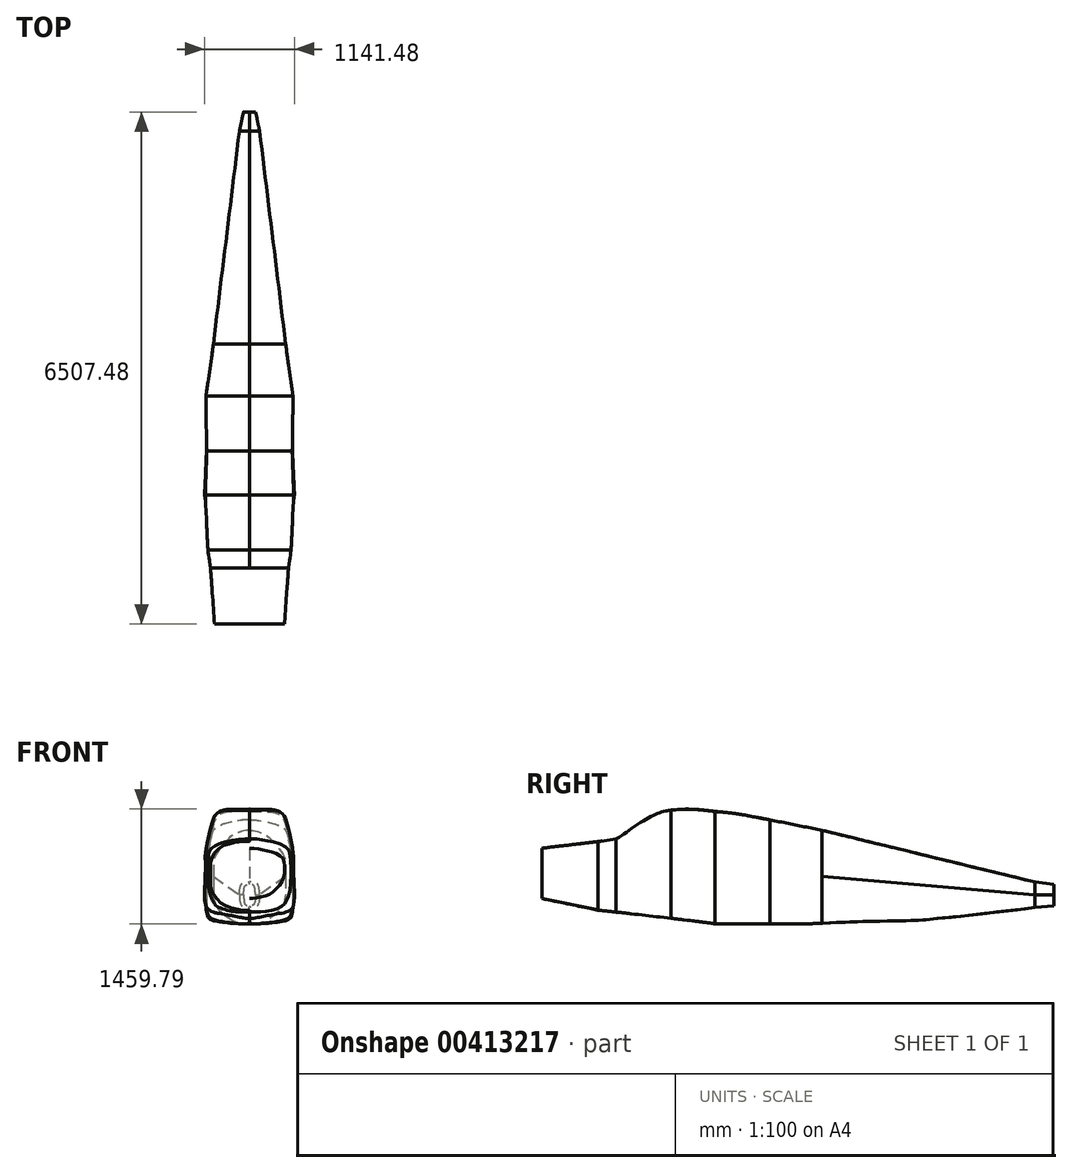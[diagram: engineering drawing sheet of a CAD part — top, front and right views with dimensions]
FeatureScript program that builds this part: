
annotation { "Feature Type Name" : "Feature", "Feature Type Description" : "" }
export const myFeature = defineFeature(function(context is Context, id is Id, definition is map)
    precondition{}
    {
        {
            var Q0;
            Q0=qCreatedBy(makeId("Right.planeOp"),FACE);
            var sketch = newSketch(context, id + "F0", { "sketchPlane" : qUnion([Q0])});
            skLineSegment(sketch, "E0.bottom", {"start": v(0, 664.6) * mm, "end": v(7102.65, 664.6) * mm});
            skLineSegment(sketch, "E0.top", {"start": v(0, -785.51) * mm, "end": v(7102.65, -785.51) * mm});
            skLineSegment(sketch, "E0.left", {"start": v(0, 664.6) * mm, "end": v(0, -785.51) * mm});
            skLineSegment(sketch, "E0.right", {"start": v(7102.65, 664.6) * mm, "end": v(7102.65, -785.51) * mm});
            skLineSegment(sketch, "E1", {"start": v(443.28, 664.6) * mm, "end": v(443.28, -785.51) * mm});
            skLineSegment(sketch, "E2", {"start": v(1215.1, 664.6) * mm, "end": v(1215.1, -785.51) * mm});
            skLineSegment(sketch, "E3", {"start": v(1422.4, 664.6) * mm, "end": v(1422.4, -785.51) * mm});
            skLineSegment(sketch, "E4", {"start": v(2120.9, 664.6) * mm, "end": v(2120.9, -785.51) * mm});
            skLineSegment(sketch, "E5", {"start": v(2679.7, -785.51) * mm, "end": v(2679.7, 664.6) * mm});
            skLineSegment(sketch, "E6", {"start": v(4038.6, -785.51) * mm, "end": v(4038.6, 664.6) * mm});
            skLineSegment(sketch, "E7", {"start": v(6743.7, -785.51) * mm, "end": v(6743.7, 664.6) * mm});
            skSolve(sketch);
        }
        {
            var Q0;
            Q0=qCreatedBy(makeId("Right.planeOp"),FACE);
            var sketch = newSketch(context, id + "F1", { "sketchPlane" : qUnion([Q0])});
            skLineSegment(sketch, "E8", {"start": v(1193.8, 265.93) * mm, "end": v(1193.8, -604.42) * mm, "construction": true});
            skPoint(sketch, "E9.0", {"position": v(2120.9, 664.6) * mm});
            skLineSegment(sketch, "E10", {"start": v(2120.9, 664.6) * mm, "end": v(2120.9, -709.04) * mm, "construction": true});
            skLineSegment(sketch, "E11", {"start": v(2681.49, 648.53) * mm, "end": v(2681.49, -773.88) * mm, "construction": true});
            skLineSegment(sketch, "E12", {"start": v(3378.2, 541.47) * mm, "end": v(3378.2, -781.53) * mm, "construction": true});
            skLineSegment(sketch, "E13", {"start": v(4038.6, 407.3) * mm, "end": v(4038.6, -774.77) * mm, "construction": true});
            skLineSegment(sketch, "E14", {"start": v(6743.7, -248.1) * mm, "end": v(6743.7, -572.47) * mm, "construction": true});
            skLineSegment(sketch, "E15", {"start": v(6985, -277.2) * mm, "end": v(6985, -542.5) * mm, "construction": true});
            skLineSegment(sketch, "E16", {"start": v(1422.4, 302.03) * mm, "end": v(1422.4, -628.4) * mm, "construction": true});
            skSolve(sketch);
        }
        {
            var Q0;
            Q0=qCreatedBy(makeId("Front.planeOp"),FACE);
            cPlane(context, id + "F2", {"entities" : qUnion([Q0]), "cplaneType" : CPlaneType.OFFSET, "offset" : 477.52 * mm, "oppositeDirection" : true, "width" : 152.4 * mm, "height" : 152.4 * mm});
        }
        {
            var Q0;
            Q0=qCreatedBy(id+"F2.planeOp",FACE);
            var sketch = newSketch(context, id + "F3", { "sketchPlane" : qUnion([Q0])});
            skLineSegment(sketch, "E17", {"start": v(0, 424.34) * mm, "end": v(0, -539.78) * mm, "construction": true});
            skFitSpline(sketch, "E18", {"points": [v(0, 182.3) * mm, v(-107.19, 174.3) * mm, v(-211.2, 152.3) * mm, v(-325.22, 122.3) * mm, v(-413.23, 66.3) * mm, v(-443.23, 0) * mm, v(-443.23, -75.73) * mm, v(-441.23, -153.74) * mm, v(-407.23, -249.75) * mm, v(-343.22, -329.76) * mm, v(-259.2, -399.77) * mm, v(-165.2, -431.77) * mm, v(-58.44, -456.1) * mm, v(0, -457.77) * mm], "startDerivative": vector(-1334.66, 9.94) * mm, "endDerivative": vector(885.54, -12.67) * mm});
            skFitSpline(sketch, "E19.MirrorCS", {"points": [v(0, 182.3) * mm, v(107.19, 174.3) * mm, v(211.2, 152.3) * mm, v(325.22, 122.3) * mm, v(413.23, 66.3) * mm, v(443.23, 0) * mm, v(443.23, -75.73) * mm, v(441.23, -153.74) * mm, v(407.23, -249.75) * mm, v(343.22, -329.76) * mm, v(259.2, -399.77) * mm, v(165.2, -431.77) * mm, v(58.44, -456.1) * mm, v(0, -457.77) * mm], "startDerivative": vector(1334.66, 9.94) * mm, "endDerivative": vector(-885.54, -12.67) * mm});
            skSolve(sketch);
        }
        {
            var Q0;
            Q0=qCreatedBy(makeId("Front.planeOp"),FACE);
            cPlane(context, id + "F4", {"entities" : qUnion([Q0]), "cplaneType" : CPlaneType.OFFSET, "offset" : 1193.8 * mm, "oppositeDirection" : true, "width" : 152.4 * mm, "height" : 152.4 * mm});
        }
        {
            var Q0;
            Q0=qCreatedBy(id+"F4.planeOp",FACE);
            var sketch = newSketch(context, id + "F5", { "sketchPlane" : qUnion([Q0])});
            skPoint(sketch, "E20.0", {"position": v(0, 265.93) * mm});
            skPoint(sketch, "E21.0", {"position": v(0, -604.42) * mm});
            skLineSegment(sketch, "E22", {"start": v(0, 497.9) * mm, "end": v(0, -830.14) * mm, "construction": true});
            skFitSpline(sketch, "E23", {"points": [v(0, 265.93) * mm, v(-117.24, 265.93) * mm, v(-218.7, 247.73) * mm, v(-365.7, 195.3) * mm, v(-467.13, 84.77) * mm, v(-493.34, -18.93) * mm, v(-494.48, -237.72) * mm, v(-492.2, -322.05) * mm, v(-473.96, -381.3) * mm, v(-394.2, -483.86) * mm, v(-291.8, -554.77) * mm, v(-118.4, -602.02) * mm, v(-65.62, -605.24) * mm, v(0, -604.42) * mm], "startDerivative": vector(-1503.76, -16.45) * mm, "endDerivative": vector(927.22, -11.34) * mm});
            skFitSpline(sketch, "E24.MirrorCS", {"points": [v(0, 265.93) * mm, v(117.24, 265.93) * mm, v(218.7, 247.73) * mm, v(365.7, 195.3) * mm, v(467.13, 84.77) * mm, v(493.34, -18.93) * mm, v(494.48, -237.72) * mm, v(492.2, -322.05) * mm, v(473.96, -381.3) * mm, v(394.2, -483.86) * mm, v(291.8, -554.77) * mm, v(118.4, -602.02) * mm, v(65.62, -605.24) * mm, v(0, -604.42) * mm], "startDerivative": vector(1503.76, -16.45) * mm, "endDerivative": vector(-927.22, -11.34) * mm});
            skSolve(sketch);
        }
        {
            var Q0;
            Q0=qCreatedBy(makeId("Right.planeOp"),FACE);
            var sketch = newSketch(context, id + "F6", { "sketchPlane" : qUnion([Q0])});
            skPoint(sketch, "E25.0", {"position": v(477.52, -457.77) * mm});
            skPoint(sketch, "E26.0", {"position": v(1193.8, -604.42) * mm});
            skLineSegment(sketch, "E27", {"start": v(477.52, -457.77) * mm, "end": v(578.9, -487.9) * mm});
            skLineSegment(sketch, "E28", {"start": v(578.9, -487.9) * mm, "end": v(709.03, -514.45) * mm});
            skLineSegment(sketch, "E29", {"start": v(709.03, -514.45) * mm, "end": v(886.96, -554.29) * mm});
            skLineSegment(sketch, "E30", {"start": v(886.96, -554.29) * mm, "end": v(1006.47, -583.5) * mm});
            skLineSegment(sketch, "E31", {"start": v(1006.47, -583.5) * mm, "end": v(1091.45, -607.4) * mm});
            skLineSegment(sketch, "E32", {"start": v(1091.45, -607.4) * mm, "end": v(1193.8, -604.42) * mm});
            skSolve(sketch);
        }
        {
            var Q0;
            Q0 = qSketchRegion(id + "F3", true);
            var Q1;
            Q1 = qSketchRegion(id + "F5", true);
            var Q2;
            Q2 = qConstructionFilter(qBodyType(qCreatedBy(id + "F6" ,EDGE), BodyType.WIRE), ConstructionObject.NO);
            loft(context, id + "F7", {"sheetProfilesArray" : [{ "sheetProfileEntities" : qUnion([Q0]) }, { "sheetProfileEntities" : qUnion([Q1]) }], "guidesArray" : [{ "guideEntities" : qUnion([Q2]), "guideDerivativeType" : LoftGuideDerivativeType.DEFAULT, "guideDerivativeMagnitude" : 1 }]});
        }
        {
            var Q0;
            Q0=qCreatedBy(makeId("Front.planeOp"),FACE);
            cPlane(context, id + "F8", {"entities" : qUnion([Q0]), "cplaneType" : CPlaneType.OFFSET, "offset" : 2120.9 * mm, "oppositeDirection" : true, "width" : 152.4 * mm, "height" : 152.4 * mm});
        }
        {
            var Q0;
            Q0=qCreatedBy(id+"F8.planeOp",FACE);
            var sketch = newSketch(context, id + "F9", { "sketchPlane" : qUnion([Q0])});
            skPoint(sketch, "E33.0", {"position": v(0, 664.6) * mm});
            skPoint(sketch, "E34.0", {"position": v(0, -709.04) * mm});
            skLineSegment(sketch, "E35", {"start": v(0, 971.77) * mm, "end": v(0, -1592.86) * mm, "construction": true});
            skFitSpline(sketch, "E36", {"points": [v(0, 664.6) * mm, v(-101.29, 664.6) * mm, v(-256.4, 664.6) * mm, v(-374.13, 647.55) * mm, v(-435.8, 602.7) * mm, v(-473.18, 499.92) * mm, v(-521.77, 320.52) * mm, v(-561.01, 81.31) * mm, v(-561.01, 21.5) * mm, v(-564.75, -225.17) * mm, v(-564.75, -511.18) * mm, v(-511.32, -608.6) * mm, v(-329.03, -655.75) * mm, v(-149.88, -690.32) * mm, v(0, -709.04) * mm], "startDerivative": vector(-1623.74, -9.76) * mm, "endDerivative": vector(2155.82, 3.58) * mm});
            skFitSpline(sketch, "E37.MirrorCS", {"points": [v(0, 664.6) * mm, v(101.29, 664.6) * mm, v(256.4, 664.6) * mm, v(374.13, 647.55) * mm, v(435.8, 602.7) * mm, v(473.18, 499.92) * mm, v(521.77, 320.52) * mm, v(561.01, 81.31) * mm, v(561.01, 21.5) * mm, v(564.75, -225.17) * mm, v(564.75, -511.18) * mm, v(511.32, -608.6) * mm, v(329.03, -655.75) * mm, v(149.88, -690.32) * mm, v(0, -709.04) * mm], "startDerivative": vector(1623.74, -9.76) * mm, "endDerivative": vector(-2155.82, 3.58) * mm});
            skSolve(sketch);
        }
        {
            var Q0;
            Q0=qCreatedBy(makeId("Front.planeOp"),FACE);
            cPlane(context, id + "F10", {"entities" : qUnion([Q0]), "cplaneType" : CPlaneType.OFFSET, "offset" : 2679.7 * mm, "oppositeDirection" : true, "width" : 152.4 * mm, "height" : 152.4 * mm});
        }
        {
            var Q0;
            Q0=qCreatedBy(id+"F10.planeOp",FACE);
            var sketch = newSketch(context, id + "F11", { "sketchPlane" : qUnion([Q0])});
            skPoint(sketch, "E38.0", {"position": v(0, 648.53) * mm});
            skPoint(sketch, "E39.0", {"position": v(0, -773.88) * mm});
            skFitSpline(sketch, "E40", {"points": [v(0, 648.53) * mm, v(-140.26, 646.75) * mm, v(-333.17, 631.31) * mm, v(-426.03, 561.67) * mm, v(-474.4, 414.64) * mm, v(-534.2, 101.76) * mm, v(-540.4, 33.51) * mm, v(-542.02, -96.63) * mm, v(-542.7, -300.13) * mm, v(-545, -544) * mm, v(-518.89, -679.55) * mm, v(-441.96, -729.72) * mm, v(-281.91, -759.82) * mm, v(-86.3, -778.97) * mm, v(0, -773.88) * mm], "startDerivative": vector(-2067.33, -24.6) * mm, "endDerivative": vector(1428.64, 166.52) * mm});
            skFitSpline(sketch, "E41.MirrorCS", {"points": [v(0, 648.53) * mm, v(140.26, 646.75) * mm, v(333.17, 631.31) * mm, v(426.03, 561.67) * mm, v(474.4, 414.64) * mm, v(534.2, 101.76) * mm, v(540.4, 33.51) * mm, v(542.02, -96.63) * mm, v(542.7, -300.13) * mm, v(545, -544) * mm, v(518.89, -679.55) * mm, v(441.96, -729.72) * mm, v(281.91, -759.82) * mm, v(86.3, -778.97) * mm, v(0, -773.88) * mm], "startDerivative": vector(2067.33, -24.6) * mm, "endDerivative": vector(-1428.64, 166.52) * mm});
            skSolve(sketch);
        }
        {
            var Q0;
            Q0=qCreatedBy(makeId("Right.planeOp"),FACE);
            var sketch = newSketch(context, id + "F12", { "sketchPlane" : qUnion([Q0])});
            skPoint(sketch, "E42.0", {"position": v(2120.9, 664.6) * mm});
            skPoint(sketch, "E43.0", {"position": v(2679.7, 648.53) * mm});
            skFitSpline(sketch, "E44", {"points": [v(2679.7, 648.53) * mm, v(2506.44, 669.53) * mm, v(2270.09, 677.5) * mm, v(2120.9, 664.6) * mm], "startDerivative": vector(-512.84, 70.22) * mm, "endDerivative": vector(-464.5, -49.21) * mm});
            skSolve(sketch);
        }
        {
            var Q0;
            Q0 = qSketchRegion(id + "F9", true);
            var Q1;
            Q1 = qSketchRegion(id + "F11", true);
            var Q2;
            Q2 = qConstructionFilter(qBodyType(qCreatedBy(id + "F12" ,EDGE), BodyType.WIRE), ConstructionObject.NO);
            loft(context, id + "F13", {"addGuides" : true, "sheetProfilesArray" : [{ "sheetProfileEntities" : qUnion([Q0]) }, { "sheetProfileEntities" : qUnion([Q1]) }], "guidesArray" : [{ "guideEntities" : qUnion([Q2]), "guideDerivativeType" : LoftGuideDerivativeType.DEFAULT, "guideDerivativeMagnitude" : 1 }]});
        }
        {
            var Q0;
            Q0=qCreatedBy(makeId("Front.planeOp"),FACE);
            cPlane(context, id + "F14", {"entities" : qUnion([Q0]), "cplaneType" : CPlaneType.OFFSET, "offset" : 3378.2 * mm, "oppositeDirection" : true, "width" : 152.4 * mm, "height" : 152.4 * mm});
        }
        {
            var Q0;
            Q0=qCreatedBy(id+"F14.planeOp",FACE);
            var sketch = newSketch(context, id + "F15", { "sketchPlane" : qUnion([Q0])});
            skPoint(sketch, "E45.0", {"position": v(0, 541.47) * mm});
            skPoint(sketch, "E46.0", {"position": v(0, -781.53) * mm});
            skFitSpline(sketch, "E47", {"points": [v(0, 541.47) * mm, v(-60.52, 541.47) * mm, v(-174.88, 526.9) * mm, v(-293.18, 499.3) * mm, v(-386.5, 462.5) * mm, v(-445.65, 427) * mm, v(-475.89, 378.37) * mm, v(-511.38, 212.75) * mm, v(-541.6, 16.9) * mm, v(-549.5, -105.34) * mm, v(-552.62, -339.82) * mm, v(-551.68, -522.73) * mm, v(-538.67, -662.15) * mm, v(-499.63, -719.78) * mm, v(-408.54, -749.52) * mm, v(-198.49, -773.69) * mm, v(0, -781.53) * mm], "startDerivative": vector(-1297.49, 46.78) * mm, "endDerivative": vector(2468.79, -52.6) * mm});
            skFitSpline(sketch, "E48.MirrorCS", {"points": [v(0, 541.47) * mm, v(60.52, 541.47) * mm, v(174.88, 526.9) * mm, v(293.18, 499.3) * mm, v(386.5, 462.5) * mm, v(445.65, 427) * mm, v(475.89, 378.37) * mm, v(511.38, 212.75) * mm, v(541.6, 16.9) * mm, v(549.5, -105.34) * mm, v(552.62, -339.82) * mm, v(551.68, -522.73) * mm, v(538.67, -662.15) * mm, v(499.63, -719.78) * mm, v(408.54, -749.52) * mm, v(198.49, -773.69) * mm, v(0, -781.53) * mm], "startDerivative": vector(1297.49, 46.78) * mm, "endDerivative": vector(-2468.79, -52.6) * mm});
            skSolve(sketch);
        }
        {
            var Q0;
            Q0=qCreatedBy(makeId("Right.planeOp"),FACE);
            var sketch = newSketch(context, id + "F16", { "sketchPlane" : qUnion([Q0])});
            skPoint(sketch, "E49.0", {"position": v(2679.7, 648.53) * mm});
            skPoint(sketch, "E50.0", {"position": v(3378.2, 541.47) * mm});
            skFitSpline(sketch, "E51", {"points": [v(2679.7, 648.53) * mm, v(2902.66, 626.6) * mm, v(3105.88, 593.1) * mm, v(3285.74, 558.17) * mm, v(3378.2, 541.47) * mm], "startDerivative": vector(795.05, -63.4) * mm, "endDerivative": vector(532.18, -90) * mm});
            skSolve(sketch);
        }
        {
            var Q0;
            Q0 = qSketchRegion(id + "F11", true);
            var Q1;
            Q1 = qSketchRegion(id + "F15", true);
            var Q2;
            Q2 = qConstructionFilter(qBodyType(qCreatedBy(id + "F16" ,EDGE), BodyType.WIRE), ConstructionObject.NO);
            loft(context, id + "F17", {"addGuides" : true, "sheetProfilesArray" : [{ "sheetProfileEntities" : qUnion([Q0]) }, { "sheetProfileEntities" : qUnion([Q1]) }], "guidesArray" : [{ "guideEntities" : qUnion([Q2]), "guideDerivativeType" : LoftGuideDerivativeType.DEFAULT, "guideDerivativeMagnitude" : 1 }]});
        }
        {
            var Q0;
            Q0=qCreatedBy(makeId("Front.planeOp"),FACE);
            cPlane(context, id + "F18", {"entities" : qUnion([Q0]), "cplaneType" : CPlaneType.OFFSET, "offset" : 4038.6 * mm, "oppositeDirection" : true, "width" : 152.4 * mm, "height" : 152.4 * mm});
        }
        {
            var Q0;
            Q0=qCreatedBy(makeId("Top.planeOp"),FACE);
            var sketch = newSketch(context, id + "F19", { "sketchPlane" : qUnion([Q0])});
            skLineSegment(sketch, "E52", {"start": v(0, 4038.6) * mm, "end": v(495.66, 4038.6) * mm, "construction": true});
            skLineSegment(sketch, "E53", {"start": v(495.66, 4038.6) * mm, "end": v(-456.85, 4038.6) * mm, "construction": true});
            skLineSegment(sketch, "E54", {"start": v(0, 6743.7) * mm, "end": v(-127, 6743.7) * mm, "construction": true});
            skLineSegment(sketch, "E55", {"start": v(0, 6743.7) * mm, "end": v(127, 6743.7) * mm, "construction": true});
            skLineSegment(sketch, "E56", {"start": v(0, 6743.7) * mm, "end": v(0, 7109.15) * mm, "construction": true});
            skLineSegment(sketch, "E57", {"start": v(0, 7001.4) * mm, "end": v(-76.2, 7001.4) * mm, "construction": true});
            skLineSegment(sketch, "E58", {"start": v(0, 7001.4) * mm, "end": v(76.2, 7001.4) * mm, "construction": true});
            skSolve(sketch);
        }
        {
            var Q0;
            Q0=qCreatedBy(id+"F18.planeOp",FACE);
            var sketch = newSketch(context, id + "F20", { "sketchPlane" : qUnion([Q0])});
            skPoint(sketch, "E59.0", {"position": v(-456.85, 0) * mm});
            skPoint(sketch, "E60.0", {"position": v(495.66, 0) * mm});
            skPoint(sketch, "E61.0", {"position": v(0, 407.3) * mm});
            skPoint(sketch, "E62.0", {"position": v(0, -774.77) * mm});
            skFitSpline(sketch, "E63", {"points": [v(0, 407.3) * mm, v(-51.47, 407.3) * mm, v(-149.27, 376.32) * mm, v(-240.24, 326.29) * mm, v(-324.39, 239.86) * mm, v(-424.46, 103.4) * mm, v(-456.85, 0) * mm, v(-456.85, -224.1) * mm, v(-456.85, -387.85) * mm, v(-424.46, -551.6) * mm, v(-347.13, -642.57) * mm, v(-247.06, -715.35) * mm, v(-142.44, -765.38) * mm, v(0, -774.77) * mm], "startDerivative": vector(-972.04, 89.96) * mm, "endDerivative": vector(1842.9, 24.98) * mm});
            skLineSegment(sketch, "E64", {"start": v(0, 407.3) * mm, "end": v(0, -774.77) * mm, "construction": true});
            skFitSpline(sketch, "E65.MirrorCS", {"points": [v(0, 407.3) * mm, v(51.47, 407.3) * mm, v(149.27, 376.32) * mm, v(240.24, 326.29) * mm, v(324.39, 239.86) * mm, v(424.46, 103.4) * mm, v(456.85, 0) * mm, v(456.85, -224.1) * mm, v(456.85, -387.85) * mm, v(424.46, -551.6) * mm, v(347.13, -642.57) * mm, v(247.06, -715.35) * mm, v(142.44, -765.38) * mm, v(0, -774.77) * mm], "startDerivative": vector(972.04, 89.96) * mm, "endDerivative": vector(-1842.9, 24.98) * mm});
            skSolve(sketch);
        }
        {
            var Q0;
            Q0 = qSketchRegion(id + "F15", true);
            var Q1;
            Q1 = qSketchRegion(id + "F20", true);
            loft(context, id + "F21", {"sheetProfilesArray" : [{ "sheetProfileEntities" : qUnion([Q0]) }, { "sheetProfileEntities" : qUnion([Q1]) }]});
        }
        {
            var Q0;
            Q0=qCreatedBy(makeId("Front.planeOp"),FACE);
            cPlane(context, id + "F22", {"entities" : qUnion([Q0]), "cplaneType" : CPlaneType.OFFSET, "offset" : 6743.7 * mm, "oppositeDirection" : true, "width" : 152.4 * mm, "height" : 152.4 * mm});
        }
        {
            var Q0;
            Q0=qCreatedBy(id+"F22.planeOp",FACE);
            var sketch = newSketch(context, id + "F23", { "sketchPlane" : qUnion([Q0])});
            skPoint(sketch, "E66.0", {"position": v(-127, 0) * mm});
            skPoint(sketch, "E67.0", {"position": v(127, 0) * mm});
            skLineSegment(sketch, "E68", {"start": v(127, 0) * mm, "end": v(127, -702.28) * mm, "construction": true});
            skLineSegment(sketch, "E69", {"start": v(-127, 0) * mm, "end": v(-127, -716.91) * mm, "construction": true});
            skLineSegment(sketch, "E70.0", {"start": v(0, -248.1) * mm, "end": v(0, -572.47) * mm, "construction": true});
            skLineSegment(sketch, "E71", {"start": v(0, -410.28) * mm, "end": v(127, -410.28) * mm, "construction": true});
            skLineSegment(sketch, "E72", {"start": v(0, -410.28) * mm, "end": v(-127, -410.28) * mm, "construction": true});
            skFitSpline(sketch, "E73", {"points": [v(-127, -410.28) * mm, v(-127, -358.46) * mm, v(-110.27, -290.6) * mm, v(-93.54, -267) * mm, v(-46.4, -253.06) * mm, v(0, -248.1) * mm], "startDerivative": vector(-7.31, 225) * mm, "endDerivative": vector(303.4, 1.02) * mm});
            skFitSpline(sketch, "E74.MirrorCS", {"points": [v(-127, -410.28) * mm, v(-127, -462.11) * mm, v(-110.27, -529.96) * mm, v(-93.54, -553.57) * mm, v(-46.4, -567.5) * mm, v(0, -572.47) * mm], "startDerivative": vector(-7.31, -225) * mm, "endDerivative": vector(303.4, -1.02) * mm});
            skFitSpline(sketch, "E75.MirrorCS", {"points": [v(127, -410.28) * mm, v(127, -358.46) * mm, v(110.27, -290.6) * mm, v(93.54, -267) * mm, v(46.4, -253.06) * mm, v(0, -248.1) * mm], "startDerivative": vector(7.31, 225) * mm, "endDerivative": vector(-303.4, 1.02) * mm});
            skFitSpline(sketch, "E76.MirrorCS", {"points": [v(127, -410.28) * mm, v(127, -462.11) * mm, v(110.27, -529.96) * mm, v(93.54, -553.57) * mm, v(46.4, -567.5) * mm, v(0, -572.47) * mm], "startDerivative": vector(7.31, -225) * mm, "endDerivative": vector(-303.4, -1.02) * mm});
            skSolve(sketch);
        }
        {
            var Q0;
            Q0=qCreatedBy(makeId("Right.planeOp"),FACE);
            var sketch = newSketch(context, id + "F24", { "sketchPlane" : qUnion([Q0])});
            skPoint(sketch, "E77.0", {"position": v(4038.6, -774.77) * mm});
            skPoint(sketch, "E78.0", {"position": v(6743.7, -572.47) * mm});
            skFitSpline(sketch, "E79", {"points": [v(4038.6, -774.77) * mm, v(4410.29, -754.03) * mm, v(5033.97, -740.56) * mm, v(5384.2, -723.04) * mm, v(6743.7, -572.47) * mm], "startDerivative": vector(1724.82, 119.31) * mm, "endDerivative": vector(4362.28, 510.96) * mm});
            skSolve(sketch);
        }
        {
            var Q0;
            Q0 = qSketchRegion(id + "F20", true);
            var Q1;
            Q1 = qSketchRegion(id + "F23", true);
            var Q2;
            Q2 = qConstructionFilter(qBodyType(qCreatedBy(id + "F24" ,EDGE), BodyType.WIRE), ConstructionObject.NO);
            var Q3;
            Q3=sQuery(id+"F23.wireOp",VERTEX,"E73.end");
            var Q4;
            Q4=sQuery(id+"F20.wireOp",VERTEX,"E61.0");
            loft(context, id + "F25", {"addGuides" : true, "sheetProfilesArray" : [{ "sheetProfileEntities" : qUnion([Q0]) }, { "sheetProfileEntities" : qUnion([Q1]) }], "guidesArray" : [{ "guideEntities" : qUnion([Q2]), "guideDerivativeType" : LoftGuideDerivativeType.DEFAULT, "guideDerivativeMagnitude" : 1 }], "matchConnections" : true, "connections" : [{ "connectionEntities" : qUnion([Q3, Q4]), "connectionEdgeQueries" : qUnion([]), "connectionEdgeParameters" : [] }]});
        }
        {
            var Q0;
            Q0=qCreatedBy(makeId("Front.planeOp"),FACE);
            cPlane(context, id + "F26", {"entities" : qUnion([Q0]), "cplaneType" : CPlaneType.OFFSET, "offset" : 6985 * mm, "oppositeDirection" : true, "width" : 152.4 * mm, "height" : 152.4 * mm});
        }
        {
            var Q0;
            Q0=qCreatedBy(id+"F26.planeOp",FACE);
            var sketch = newSketch(context, id + "F27", { "sketchPlane" : qUnion([Q0])});
            skPoint(sketch, "E80.0", {"position": v(76.2, 0) * mm});
            skPoint(sketch, "E81.0", {"position": v(-76.2, 0) * mm});
            skPoint(sketch, "E82.0", {"position": v(0, -277.2) * mm});
            skPoint(sketch, "E83.0", {"position": v(0, -542.5) * mm});
            skLineSegment(sketch, "E84", {"start": v(76.2, 0) * mm, "end": v(76.2, -591.8) * mm, "construction": true});
            skLineSegment(sketch, "E85", {"start": v(-76.2, 0) * mm, "end": v(-76.2, -595.17) * mm, "construction": true});
            skLineSegment(sketch, "E86", {"start": v(-76.2, -277.2) * mm, "end": v(76.2, -277.2) * mm, "construction": true});
            skLineSegment(sketch, "E87", {"start": v(-76.2, -542.5) * mm, "end": v(76.2, -542.5) * mm, "construction": true});
            skLineSegment(sketch, "E88", {"start": v(0, -256.27) * mm, "end": v(0, -569.5) * mm, "construction": true});
            skLineSegment(sketch, "E89", {"start": v(0, -412.89) * mm, "end": v(-76.2, -412.89) * mm, "construction": true});
            skLineSegment(sketch, "E90", {"start": v(-76.2, -412.89) * mm, "end": v(76.2, -412.89) * mm, "construction": true});
            skFitSpline(sketch, "E91", {"points": [v(-76.2, -412.89) * mm, v(-75.26, -396.04) * mm, v(-71.85, -359) * mm, v(-67.74, -324.3) * mm, v(-52.2, -292.78) * mm, v(-25.72, -280.45) * mm, v(0, -277.2) * mm], "startDerivative": vector(4.69, 118.94) * mm, "endDerivative": vector(161.84, 13.25) * mm});
            skFitSpline(sketch, "E92.MirrorCS", {"points": [v(-76.2, -412.89) * mm, v(-75.26, -429.73) * mm, v(-71.85, -466.77) * mm, v(-67.74, -501.48) * mm, v(-52.2, -533) * mm, v(-25.72, -545.32) * mm, v(0, -548.57) * mm], "startDerivative": vector(4.69, -118.94) * mm, "endDerivative": vector(161.84, -13.25) * mm});
            skFitSpline(sketch, "E93.MirrorCS", {"points": [v(76.2, -412.89) * mm, v(75.26, -396.04) * mm, v(71.85, -359) * mm, v(67.74, -324.3) * mm, v(52.2, -292.78) * mm, v(25.72, -280.45) * mm, v(0, -277.2) * mm], "startDerivative": vector(-4.69, 118.94) * mm, "endDerivative": vector(-161.84, 13.25) * mm});
            skFitSpline(sketch, "E94.MirrorCS", {"points": [v(76.2, -412.89) * mm, v(75.26, -429.73) * mm, v(71.85, -466.77) * mm, v(67.74, -501.48) * mm, v(52.2, -533) * mm, v(25.72, -545.32) * mm, v(0, -548.57) * mm], "startDerivative": vector(-4.69, -118.94) * mm, "endDerivative": vector(-161.84, -13.25) * mm});
            skSolve(sketch);
        }
        {
            var Q0;
            Q0 = qSketchRegion(id + "F27", true);
            var Q1;
            Q1 = qSketchRegion(id + "F23", true);
            loft(context, id + "F28", {"sheetProfilesArray" : [{ "sheetProfileEntities" : qUnion([Q0]) }, { "sheetProfileEntities" : qUnion([Q1]) }]});
        }
        {
            var Q0;
            Q0=qCreatedBy(makeId("Front.planeOp"),FACE);
            cPlane(context, id + "F29", {"entities" : qUnion([Q0]), "cplaneType" : CPlaneType.OFFSET, "offset" : 1422.4 * mm, "oppositeDirection" : true, "width" : 152.4 * mm, "height" : 152.4 * mm});
        }
        {
            var Q0;
            Q0=qCreatedBy(id+"F29.planeOp",FACE);
            var sketch = newSketch(context, id + "F30", { "sketchPlane" : qUnion([Q0])});
            skPoint(sketch, "E95.0", {"position": v(0, 302.03) * mm});
            skPoint(sketch, "E96.0", {"position": v(0, -628.4) * mm});
            skLineSegment(sketch, "E97", {"start": v(0, 1062.38) * mm, "end": v(0, -1195.84) * mm, "construction": true});
            skFitSpline(sketch, "E98", {"points": [v(0, -628.4) * mm, v(-139.55, -628.4) * mm, v(-281.68, -605.19) * mm, v(-410.82, -557.81) * mm, v(-456.99, -504.25) * mm, v(-500.6, -400.66) * mm, v(-527.87, -184.4) * mm, v(-520.6, 50.06) * mm, v(-490.42, 170.37) * mm, v(-347.2, 249.13) * mm, v(-175.36, 286.73) * mm, v(0, 302.03) * mm], "startDerivative": vector(-1156.34, -42.11) * mm, "endDerivative": vector(2450.74, 86.5) * mm});
            skFitSpline(sketch, "E99.MirrorCS", {"points": [v(0, -628.4) * mm, v(139.55, -628.4) * mm, v(281.68, -605.19) * mm, v(410.82, -557.81) * mm, v(456.99, -504.25) * mm, v(500.6, -400.66) * mm, v(527.87, -184.4) * mm, v(520.6, 50.06) * mm, v(490.42, 170.37) * mm, v(347.2, 249.13) * mm, v(175.36, 286.73) * mm, v(0, 302.03) * mm], "startDerivative": vector(1156.34, -42.11) * mm, "endDerivative": vector(-2450.74, 86.5) * mm});
            skSolve(sketch);
        }
        {
            var Q0;
            Q0=qCreatedBy(makeId("Right.planeOp"),FACE);
            var sketch = newSketch(context, id + "F31", { "sketchPlane" : qUnion([Q0])});
            skPoint(sketch, "E100.0", {"position": v(1193.8, 265.93) * mm});
            skPoint(sketch, "E101.0", {"position": v(1422.4, 302.03) * mm});
            skFitSpline(sketch, "E102", {"points": [v(1193.8, 265.93) * mm, v(1211.67, 268.52) * mm, v(1306, 279.68) * mm, v(1370.55, 291.02) * mm, v(1422.4, 302.03) * mm], "startDerivative": vector(94.22, 15.6) * mm, "endDerivative": vector(209.57, 45.16) * mm, "construction": true});
            skSolve(sketch);
        }
        {
            var Q0;
            Q0 = qSketchRegion(id + "F30", true);
            var Q1;
            Q1 = qSketchRegion(id + "F5", true);
            var Q2;
            Q2 = qConstructionFilter(qBodyType(qCreatedBy(id + "F31" ,EDGE), BodyType.WIRE), ConstructionObject.NO);
            loft(context, id + "F32", {"addGuides" : true, "sheetProfilesArray" : [{ "sheetProfileEntities" : qUnion([Q0]) }, { "sheetProfileEntities" : qUnion([Q1]) }], "guidesArray" : [{ "guideEntities" : qUnion([Q2]), "guideDerivativeType" : LoftGuideDerivativeType.DEFAULT, "guideDerivativeMagnitude" : 1 }]});
        }
        {
            var Q0;
            Q0=qCreatedBy(makeId("Right.planeOp"),FACE);
            var sketch = newSketch(context, id + "F33", { "sketchPlane" : qUnion([Q0])});
            skPoint(sketch, "E103.0", {"position": v(1422.4, 302.03) * mm});
            skPoint(sketch, "E104.0", {"position": v(2120.9, 664.6) * mm});
            skFitSpline(sketch, "E105", {"points": [v(1422.4, 302.03) * mm, v(1475.4, 331.23) * mm, v(1639, 446.53) * mm, v(1860.72, 583.5) * mm, v(1975.04, 634.75) * mm, v(2120.9, 664.6) * mm], "startDerivative": vector(609.54, 355.46) * mm, "endDerivative": vector(866.03, 93.92) * mm});
            skSolve(sketch);
        }
        {
            var Q0;
            Q0 = qSketchRegion(id + "F30", true);
            var Q1;
            Q1 = qSketchRegion(id + "F9", true);
            var Q2;
            Q2 = qConstructionFilter(qBodyType(qCreatedBy(id + "F33" ,EDGE), BodyType.WIRE), ConstructionObject.NO);
            loft(context, id + "F34", {"addGuides" : true, "sheetProfilesArray" : [{ "sheetProfileEntities" : qUnion([Q0]) }, { "sheetProfileEntities" : qUnion([Q1]) }], "guidesArray" : [{ "guideEntities" : qUnion([Q2]), "guideDerivativeType" : LoftGuideDerivativeType.DEFAULT, "guideDerivativeMagnitude" : 1 }]});
        }
    });
